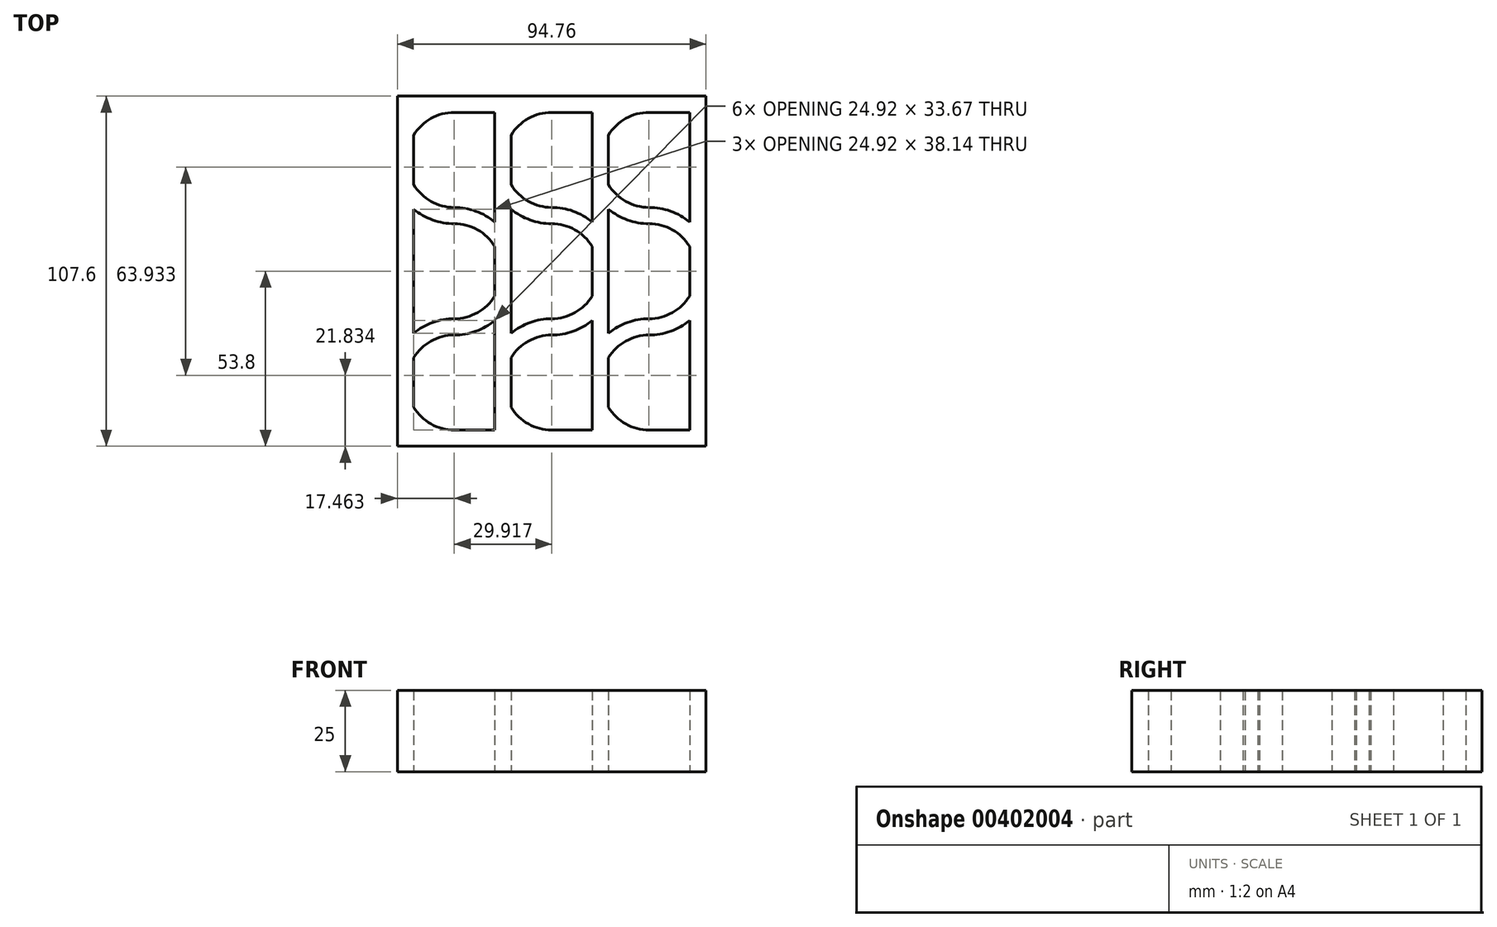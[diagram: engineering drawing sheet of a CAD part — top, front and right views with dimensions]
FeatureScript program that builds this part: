
annotation { "Feature Type Name" : "Feature", "Feature Type Description" : "" }
export const myFeature = defineFeature(function(context is Context, id is Id, definition is map)
    precondition{}
    {
        {
            var Q0;
            Q0=qCreatedBy(makeId("Top.planeOp"),FACE);
            var sketch = newSketch(context, id + "F0", { "sketchPlane" : qUnion([Q0])});
            skLineSegment(sketch, "E0.bottom", {"start": v(-47.37, 53.8) * mm, "end": v(47.38, 53.8) * mm});
            skLineSegment(sketch, "E0.top", {"start": v(-47.38, -53.8) * mm, "end": v(47.37, -53.8) * mm});
            skLineSegment(sketch, "E0.left", {"start": v(-47.37, 53.8) * mm, "end": v(-47.38, -53.8) * mm});
            skLineSegment(sketch, "E0.right", {"start": v(47.38, 53.8) * mm, "end": v(47.37, -53.8) * mm});
            skPoint(sketch, "E0.middle", {"position": v(0, 0) * mm});
            skLineSegment(sketch, "E1.bottom", {"start": v(-29.92, -48.8) * mm, "end": v(-17.46, -48.8) * mm});
            skLineSegment(sketch, "E1.top", {"start": v(-29.92, 48.8) * mm, "end": v(-17.46, 48.8) * mm});
            skLineSegment(sketch, "E1.left", {"start": v(-42.38, -41.81) * mm, "end": v(-42.38, -26.59) * mm});
            skLineSegment(sketch, "E1.right", {"start": v(42.38, -48.8) * mm, "end": v(42.38, -15.13) * mm});
            skLineSegment(sketch, "E2", {"start": v(-69.21, 0) * mm, "end": v(80.92, 0) * mm, "construction": true});
            skLineSegment(sketch, "E3", {"start": v(0, -107.17) * mm, "end": v(0, 107.27) * mm, "construction": true});
            skLineSegment(sketch, "E4.left", {"start": v(12.46, -48.8) * mm, "end": v(12.46, -15.13) * mm});
            skLineSegment(sketch, "E4.right", {"start": v(17.46, -41.81) * mm, "end": v(17.46, -26.59) * mm});
            skPoint(sketch, "E4.middle", {"position": v(14.96, 0) * mm});
            skLineSegment(sketch, "E5.left", {"start": v(-17.46, -48.8) * mm, "end": v(-17.46, -15.13) * mm});
            skLineSegment(sketch, "E5.right", {"start": v(-12.46, -41.81) * mm, "end": v(-12.46, -26.59) * mm});
            skPoint(sketch, "E5.middle", {"position": v(-14.96, 0) * mm});
            skLineSegment(sketch, "E6", {"start": v(-12.46, 0) * mm, "end": v(12.46, 0) * mm, "construction": true});
            skLineSegment(sketch, "E7", {"start": v(12.46, 0) * mm, "end": v(17.46, 0) * mm, "construction": true});
            skLineSegment(sketch, "E8", {"start": v(14.96, -80.06) * mm, "end": v(14.96, 80.62) * mm, "construction": true});
            skLineSegment(sketch, "E9", {"start": v(-14.96, -80.23) * mm, "end": v(-14.96, 80.46) * mm, "construction": true});
            skLineSegment(sketch, "E10", {"start": v(-47.38, 0) * mm, "end": v(-42.38, 0) * mm, "construction": true});
            skLineSegment(sketch, "E11", {"start": v(-44.88, 0) * mm, "end": v(-44.87, -80.57) * mm, "construction": true});
            skLineSegment(sketch, "E12", {"start": v(-44.88, 0) * mm, "end": v(-44.88, 79.28) * mm, "construction": true});
            skLineSegment(sketch, "E13", {"start": v(42.38, 0) * mm, "end": v(47.38, 0) * mm, "construction": true});
            skLineSegment(sketch, "E14", {"start": v(44.88, 0) * mm, "end": v(44.88, -77.54) * mm, "construction": true});
            skLineSegment(sketch, "E15", {"start": v(44.88, 0) * mm, "end": v(44.88, 80.96) * mm, "construction": true});
            skLineSegment(sketch, "E16", {"start": v(-42.38, 0) * mm, "end": v(-17.46, 0) * mm, "construction": true});
            skLineSegment(sketch, "E17", {"start": v(-29.92, 0) * mm, "end": v(-29.92, -79.56) * mm, "construction": true});
            skLineSegment(sketch, "E18", {"start": v(-29.92, 0) * mm, "end": v(-29.92, 81.63) * mm, "construction": true});
            skLineSegment(sketch, "E19", {"start": v(-29.92, -47.38) * mm, "end": v(-29.92, -42.38) * mm, "construction": true});
            skLineSegment(sketch, "E20", {"start": v(17.46, 0) * mm, "end": v(42.38, 0) * mm, "construction": true});
            skLineSegment(sketch, "E21", {"start": v(29.92, 0) * mm, "end": v(29.92, 117.06) * mm, "construction": true});
            skLineSegment(sketch, "E22", {"start": v(29.92, 0) * mm, "end": v(29.92, -66.33) * mm, "construction": true});
            skArc(sketch, "E23", {"start": v(29.92, -14.6) * mm, "mid": v(37.06, -12.73) * mm, "end": v(42.38, -7.61) * mm});
            skArc(sketch, "E24", {"start": v(29.92, -19.6) * mm, "mid": v(36.53, -18.45) * mm, "end": v(42.38, -15.13) * mm});
            skArc(sketch, "E25", {"start": v(17.46, 26.59) * mm, "mid": v(22.77, 21.47) * mm, "end": v(29.92, 19.6) * mm});
            skArc(sketch, "E26", {"start": v(17.46, -41.81) * mm, "mid": v(22.77, -46.93) * mm, "end": v(29.92, -48.8) * mm});
            skArc(sketch, "E27", {"start": v(29.92, -14.6) * mm, "mid": v(23.3, -15.75) * mm, "end": v(17.46, -19.07) * mm});
            skArc(sketch, "E28.trimOffspring", {"start": v(29.92, -19.6) * mm, "mid": v(22.77, -21.47) * mm, "end": v(17.46, -26.59) * mm});
            skArc(sketch, "E29.trimOffspring", {"start": v(42.38, 15.13) * mm, "mid": v(36.53, 18.45) * mm, "end": v(29.92, 19.6) * mm});
            skArc(sketch, "E30.trimOffspring", {"start": v(42.38, 7.61) * mm, "mid": v(37.06, 12.73) * mm, "end": v(29.92, 14.6) * mm});
            skArc(sketch, "E31.trimOffspring", {"start": v(17.46, 19.07) * mm, "mid": v(23.3, 15.75) * mm, "end": v(29.92, 14.6) * mm});
            skArc(sketch, "E32.trimOffspring", {"start": v(29.92, 48.8) * mm, "mid": v(22.77, 46.93) * mm, "end": v(17.46, 41.81) * mm});
            skLineSegment(sketch, "E33", {"start": v(29.92, -19.6) * mm, "end": v(29.92, -14.6) * mm, "construction": true});
            skArc(sketch, "E34.MirrorCS", {"start": v(-12.46, -41.81) * mm, "mid": v(-7.14, -46.93) * mm, "end": v(0, -48.8) * mm});
            skArc(sketch, "E35.MirrorCS", {"start": v(0, -19.6) * mm, "mid": v(-7.14, -21.47) * mm, "end": v(-12.46, -26.59) * mm});
            skArc(sketch, "E36.MirrorCS", {"start": v(0, -19.6) * mm, "mid": v(6.62, -18.45) * mm, "end": v(12.46, -15.13) * mm});
            skArc(sketch, "E37.MirrorCS", {"start": v(0, -14.6) * mm, "mid": v(7.14, -12.73) * mm, "end": v(12.46, -7.61) * mm});
            skArc(sketch, "E38.MirrorCS", {"start": v(0, -14.6) * mm, "mid": v(-6.62, -15.75) * mm, "end": v(-12.46, -19.07) * mm});
            skArc(sketch, "E39.MirrorCS", {"start": v(12.46, 7.61) * mm, "mid": v(7.14, 12.73) * mm, "end": v(0, 14.6) * mm});
            skArc(sketch, "E40.MirrorCS", {"start": v(-12.46, 19.07) * mm, "mid": v(-6.62, 15.75) * mm, "end": v(0, 14.6) * mm});
            skArc(sketch, "E41.MirrorCS", {"start": v(12.46, 15.13) * mm, "mid": v(6.62, 18.45) * mm, "end": v(0, 19.6) * mm});
            skArc(sketch, "E42.MirrorCS", {"start": v(-12.46, 26.59) * mm, "mid": v(-7.14, 21.47) * mm, "end": v(0, 19.6) * mm});
            skArc(sketch, "E43.MirrorCS", {"start": v(0, 48.8) * mm, "mid": v(-7.14, 46.93) * mm, "end": v(-12.46, 41.81) * mm});
            skPoint(sketch, "E44.MirrorCS.end.orphan", {"position": v(0, -48.8) * mm});
            skPoint(sketch, "E44.MirrorCS.start.orphan", {"position": v(12.46, -41.81) * mm});
            skPoint(sketch, "E45.MirrorCS.end.orphan", {"position": v(12.46, -26.59) * mm});
            skPoint(sketch, "E45.MirrorCS.start.orphan", {"position": v(0, -19.6) * mm});
            skPoint(sketch, "E46.orphan", {"position": v(0, -14.6) * mm});
            skPoint(sketch, "E47.MirrorCS.end.orphan", {"position": v(12.46, -19.07) * mm});
            skPoint(sketch, "E48.MirrorCS.end.orphan", {"position": v(-12.46, -15.13) * mm});
            skPoint(sketch, "E49.MirrorCS.end.orphan", {"position": v(-12.46, -7.61) * mm});
            skPoint(sketch, "E50.MirrorCS.end.orphan", {"position": v(0, 14.6) * mm});
            skPoint(sketch, "E50.MirrorCS.start.orphan", {"position": v(-12.46, 7.61) * mm});
            skPoint(sketch, "E51.orphan", {"position": v(-12.46, 15.13) * mm});
            skPoint(sketch, "E52.orphan", {"position": v(12.46, 19.07) * mm});
            skPoint(sketch, "E53.MirrorCS.end.orphan", {"position": v(0, 19.6) * mm});
            skPoint(sketch, "E54.MirrorCS.start.orphan", {"position": v(12.46, 26.59) * mm});
            skPoint(sketch, "E55.MirrorCS.end.orphan", {"position": v(12.46, 41.81) * mm});
            skPoint(sketch, "E55.MirrorCS.start.orphan", {"position": v(0, 48.8) * mm});
            skArc(sketch, "E56.MirrorCS", {"start": v(-42.38, -41.81) * mm, "mid": v(-37.06, -46.93) * mm, "end": v(-29.92, -48.8) * mm});
            skArc(sketch, "E57.MirrorCS", {"start": v(-29.92, -19.6) * mm, "mid": v(-37.06, -21.47) * mm, "end": v(-42.37, -26.59) * mm});
            skArc(sketch, "E58.MirrorCS", {"start": v(-29.92, -19.6) * mm, "mid": v(-23.3, -18.45) * mm, "end": v(-17.46, -15.13) * mm});
            skArc(sketch, "E59.MirrorCS", {"start": v(-29.92, -14.6) * mm, "mid": v(-22.77, -12.73) * mm, "end": v(-17.46, -7.61) * mm});
            skArc(sketch, "E60.MirrorCS", {"start": v(-29.92, -14.6) * mm, "mid": v(-36.53, -15.75) * mm, "end": v(-42.37, -19.07) * mm});
            skArc(sketch, "E61.MirrorCS", {"start": v(-17.46, 7.61) * mm, "mid": v(-22.77, 12.73) * mm, "end": v(-29.92, 14.6) * mm});
            skArc(sketch, "E62.MirrorCS", {"start": v(-42.37, 19.07) * mm, "mid": v(-36.53, 15.75) * mm, "end": v(-29.92, 14.6) * mm});
            skArc(sketch, "E63.MirrorCS", {"start": v(-17.46, 15.13) * mm, "mid": v(-23.3, 18.45) * mm, "end": v(-29.92, 19.6) * mm});
            skArc(sketch, "E64.MirrorCS", {"start": v(-42.38, 26.59) * mm, "mid": v(-37.06, 21.47) * mm, "end": v(-29.92, 19.6) * mm});
            skArc(sketch, "E65.MirrorCS", {"start": v(-29.92, 48.8) * mm, "mid": v(-37.06, 46.93) * mm, "end": v(-42.37, 41.81) * mm});
            skPoint(sketch, "E66.MirrorCS.end.orphan", {"position": v(-29.92, -48.8) * mm});
            skPoint(sketch, "E66.MirrorCS.start.orphan", {"position": v(-17.46, -41.81) * mm});
            skPoint(sketch, "E67.MirrorCS.end.orphan", {"position": v(-17.46, -26.59) * mm});
            skPoint(sketch, "E67.MirrorCS.start.orphan", {"position": v(-29.92, -19.6) * mm});
            skPoint(sketch, "E68.orphan", {"position": v(-17.46, -19.07) * mm});
            skPoint(sketch, "E69.MirrorCS.start.orphan", {"position": v(-29.92, -14.6) * mm});
            skPoint(sketch, "E70.MirrorCS.end.orphan", {"position": v(-42.38, -15.13) * mm});
            skPoint(sketch, "E71.MirrorCS.end.orphan", {"position": v(-42.38, -7.61) * mm});
            skPoint(sketch, "E72.MirrorCS.end.orphan", {"position": v(-29.92, 14.6) * mm});
            skPoint(sketch, "E72.MirrorCS.start.orphan", {"position": v(-42.38, 7.61) * mm});
            skPoint(sketch, "E73.orphan", {"position": v(-42.38, 15.13) * mm});
            skPoint(sketch, "E74.MirrorCS.end.orphan", {"position": v(-29.92, 19.6) * mm});
            skPoint(sketch, "E75.MirrorCS.start.orphan", {"position": v(-17.46, 19.07) * mm});
            skPoint(sketch, "E76.MirrorCS.end.orphan", {"position": v(-17.46, 41.81) * mm});
            skPoint(sketch, "E76.MirrorCS.start.orphan", {"position": v(-29.92, 48.8) * mm});
            skPoint(sketch, "E77.MirrorCS.start.orphan", {"position": v(-17.46, 26.59) * mm});
            skPoint(sketch, "E78.orphan", {"position": v(-42.38, -48.8) * mm});
            skPoint(sketch, "E79.orphan", {"position": v(-42.37, 48.8) * mm});
            skLineSegment(sketch, "E80.trimOffspring", {"start": v(-17.46, -7.61) * mm, "end": v(-17.46, 7.61) * mm});
            skLineSegment(sketch, "E81.trimOffspring", {"start": v(-17.46, 15.13) * mm, "end": v(-17.46, 48.8) * mm});
            skLineSegment(sketch, "E82.trimOffspring", {"start": v(-42.38, -19.07) * mm, "end": v(-42.38, 19.07) * mm});
            skLineSegment(sketch, "E83.trimOffspring", {"start": v(-42.38, 26.59) * mm, "end": v(-42.38, 41.81) * mm});
            skLineSegment(sketch, "E84.trimOffspring", {"start": v(0, -48.8) * mm, "end": v(12.46, -48.8) * mm});
            skLineSegment(sketch, "E85.trimOffspring", {"start": v(-12.46, -19.07) * mm, "end": v(-12.46, 19.07) * mm});
            skLineSegment(sketch, "E86.trimOffspring", {"start": v(-12.46, 26.59) * mm, "end": v(-12.46, 41.81) * mm});
            skLineSegment(sketch, "E87.trimOffspring", {"start": v(12.46, -7.61) * mm, "end": v(12.46, 7.61) * mm});
            skLineSegment(sketch, "E88.trimOffspring", {"start": v(12.46, 15.13) * mm, "end": v(12.46, 48.8) * mm});
            skLineSegment(sketch, "E89.trimOffspring", {"start": v(0, 48.8) * mm, "end": v(12.46, 48.8) * mm});
            skPoint(sketch, "E90.orphan", {"position": v(-12.46, -48.8) * mm});
            skPoint(sketch, "E5.top.end.orphan", {"position": v(-12.46, 48.8) * mm});
            skLineSegment(sketch, "E91.trimOffspring", {"start": v(29.92, -48.8) * mm, "end": v(42.38, -48.8) * mm});
            skPoint(sketch, "E92.orphan", {"position": v(17.46, -48.8) * mm});
            skLineSegment(sketch, "E93.trimOffspring", {"start": v(17.46, -19.07) * mm, "end": v(17.46, 19.07) * mm});
            skLineSegment(sketch, "E94.trimOffspring", {"start": v(42.38, -7.61) * mm, "end": v(42.38, 7.61) * mm});
            skLineSegment(sketch, "E95.trimOffspring", {"start": v(17.46, 26.59) * mm, "end": v(17.46, 41.81) * mm});
            skLineSegment(sketch, "E96.trimOffspring", {"start": v(42.38, 15.13) * mm, "end": v(42.38, 48.8) * mm});
            skLineSegment(sketch, "E97.trimOffspring", {"start": v(29.92, 48.8) * mm, "end": v(42.37, 48.8) * mm});
            skPoint(sketch, "E98.orphan", {"position": v(17.46, 48.8) * mm});
            skSolve(sketch);
        }
        {
            var Q0;
            Q0 = qSketchRegion(id + "F0", true);
            extrude(context, id + "F1", {"entities" : qUnion([Q0]), "depth" : 25 * mm});
        }
    });
